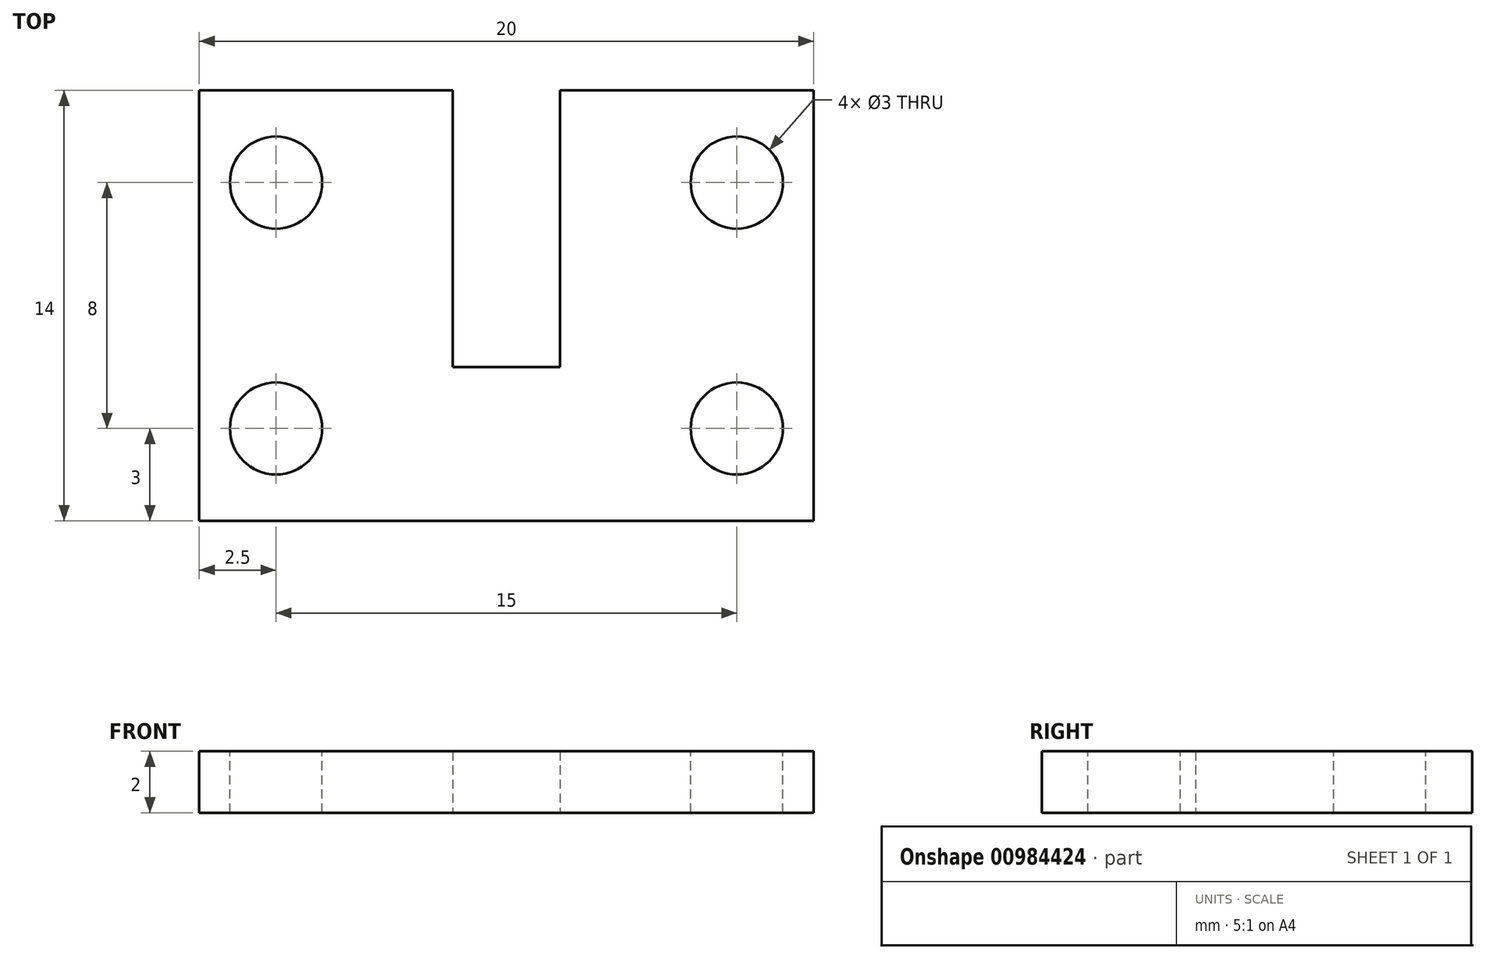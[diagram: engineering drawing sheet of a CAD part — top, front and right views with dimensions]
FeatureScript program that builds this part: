
annotation { "Feature Type Name" : "Feature", "Feature Type Description" : "" }
export const myFeature = defineFeature(function(context is Context, id is Id, definition is map)
    precondition{}
    {
        {
            var Q0;
            Q0=qCreatedBy(makeId("Top.planeOp"),FACE);
            var sketch = newSketch(context, id + "F0", { "sketchPlane" : qUnion([Q0])});
            skLineSegment(sketch, "E0.bottom", {"start": v(10, -7) * mm, "end": v(-10, -7) * mm});
            skLineSegment(sketch, "E0.top", {"start": v(10, 7) * mm, "end": v(-10, 7) * mm});
            skLineSegment(sketch, "E0.left", {"start": v(10, -7) * mm, "end": v(10, 7) * mm});
            skLineSegment(sketch, "E0.right", {"start": v(-10, -7) * mm, "end": v(-10, 7) * mm});
            skPoint(sketch, "E0.middle", {"position": v(0, 0) * mm});
            skSolve(sketch);
        }
        {
            var Q0;
            Q0 = qSketchRegion(id + "F0", true);
            extrude(context, id + "F1", {"entities" : qUnion([Q0]), "depth" : 2 * mm, "offsetDistance" : 25 * mm});
        }
        {
            var Q0;
            Q0=makeQuery(id+"F1.opExtrude","CAP_FACE",FACE,{"disambiguationData":[OSD([sQuery(id+"F0.wireOp",EDGE,"E0.bottom"),sQuery(id+"F0.wireOp",EDGE,"E0.top"),sQuery(id+"F0.wireOp",EDGE,"E0.left"),sQuery(id+"F0.wireOp",EDGE,"E0.right")])],"isStart":false});
            var sketch = newSketch(context, id + "F2", { "sketchPlane" : qUnion([Q0])});
            skLineSegment(sketch, "E1", {"start": v(-10, 7) * mm, "end": v(-5, 7) * mm, "construction": true});
            skLineSegment(sketch, "E2", {"start": v(5, 7) * mm, "end": v(10, 7) * mm, "construction": true});
            skLineSegment(sketch, "E3", {"start": v(10, -7) * mm, "end": v(5, -7) * mm, "construction": true});
            skLineSegment(sketch, "E4", {"start": v(-5, -7) * mm, "end": v(-10, -7) * mm, "construction": true});
            skLineSegment(sketch, "E5", {"start": v(5, -7) * mm, "end": v(10, -7) * mm, "construction": true});
            skLineSegment(sketch, "E6", {"start": v(-7.5, 7) * mm, "end": v(-7.5, -7) * mm, "construction": true});
            skLineSegment(sketch, "E7", {"start": v(7.5, 7) * mm, "end": v(7.5, -7) * mm, "construction": true});
            skLineSegment(sketch, "E8", {"start": v(-7.5, 7) * mm, "end": v(-7.5, 4) * mm, "construction": true});
            skLineSegment(sketch, "E9", {"start": v(7.5, -7) * mm, "end": v(7.5, -4) * mm, "construction": true});
            skLineSegment(sketch, "E10", {"start": v(-7.5, -7) * mm, "end": v(-7.5, -4) * mm, "construction": true});
            skLineSegment(sketch, "E11", {"start": v(7.5, 7) * mm, "end": v(7.5, 4) * mm, "construction": true});
            skCircle(sketch, "E12", {"center": v(-7.5, 4) * mm, "radius": 1.5 * mm});
            skCircle(sketch, "E13", {"center": v(-7.5, -4) * mm, "radius": 1.5 * mm});
            skCircle(sketch, "E14", {"center": v(7.5, -4) * mm, "radius": 1.5 * mm});
            skCircle(sketch, "E15", {"center": v(7.5, 4) * mm, "radius": 1.5 * mm});
            skSolve(sketch);
        }
        {
            var Q0;
            Q0 = qSketchRegion(id + "F2", true);
            extrude(context, id + "F3", {"entities" : qUnion([Q0]), "operationType" : NewBodyOperationType.REMOVE, "oppositeDirection" : true, "depth" : 2 * mm, "offsetDistance" : 25 * mm});
        }
        {
            var Q0;
            Q0=makeQuery(id+"F1.opExtrude","CAP_FACE",FACE,{"disambiguationData":[OSD([sQuery(id+"F0.wireOp",EDGE,"E0.bottom"),sQuery(id+"F0.wireOp",EDGE,"E0.top"),sQuery(id+"F0.wireOp",EDGE,"E0.left"),sQuery(id+"F0.wireOp",EDGE,"E0.right")])],"isStart":true});
            var sketch = newSketch(context, id + "F4", { "sketchPlane" : qUnion([Q0])});
            skLineSegment(sketch, "E16", {"start": v(0, 7) * mm, "end": v(0, 2) * mm, "construction": true});
            skLineSegment(sketch, "E17", {"start": v(0, 2) * mm, "end": v(-1.75, 2) * mm, "construction": true});
            skLineSegment(sketch, "E18", {"start": v(-1.75, 2) * mm, "end": v(1.75, 2) * mm});
            skLineSegment(sketch, "E19", {"start": v(1.75, 2) * mm, "end": v(1.75, -7) * mm});
            skLineSegment(sketch, "E20", {"start": v(1.75, -7) * mm, "end": v(-1.75, -7) * mm});
            skLineSegment(sketch, "E21", {"start": v(-1.75, -7) * mm, "end": v(-1.75, 2) * mm});
            skSolve(sketch);
        }
        {
            var Q0;
            Q0 = qSketchRegion(id + "F4", true);
            extrude(context, id + "F5", {"entities" : qUnion([Q0]), "operationType" : NewBodyOperationType.REMOVE, "oppositeDirection" : true, "depth" : 2 * mm, "offsetDistance" : 25 * mm});
        }
    });
